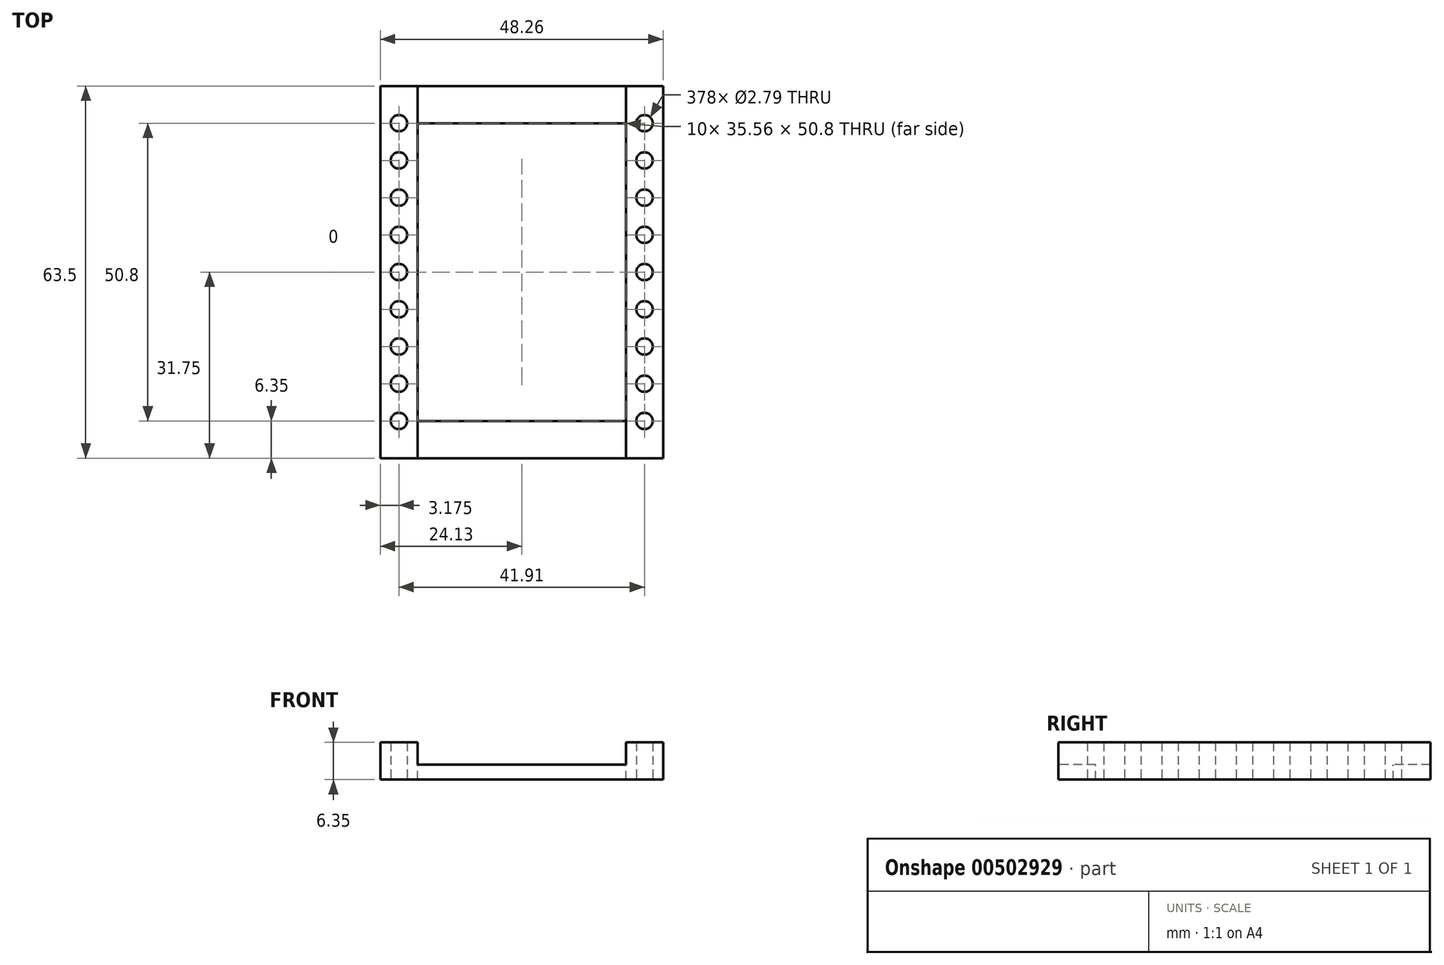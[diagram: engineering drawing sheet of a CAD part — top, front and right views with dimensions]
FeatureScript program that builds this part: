
annotation { "Feature Type Name" : "Feature", "Feature Type Description" : "" }
export const myFeature = defineFeature(function(context is Context, id is Id, definition is map)
    precondition{}
    {
        {
            var Q0;
            Q0=qCreatedBy(makeId("Top.planeOp"),FACE);
            var sketch = newSketch(context, id + "F0", { "sketchPlane" : qUnion([Q0])});
            skCircle(sketch, "E0", {"center": v(-20.96, 0) * mm, "radius": 1.4 * mm});
            skCircle(sketch, "E1", {"center": v(20.96, 0) * mm, "radius": 1.4 * mm});
            skCircle(sketch, "E2.0.1.0", {"center": v(-20.96, 6.35) * mm, "radius": 1.4 * mm});
            skCircle(sketch, "E2.0.1.1", {"center": v(20.96, 6.35) * mm, "radius": 1.4 * mm});
            skCircle(sketch, "E2.0.2.0", {"center": v(-20.96, 12.7) * mm, "radius": 1.4 * mm});
            skCircle(sketch, "E2.0.2.1", {"center": v(20.96, 12.7) * mm, "radius": 1.4 * mm});
            skCircle(sketch, "E2.0.3.0", {"center": v(-20.96, 19.05) * mm, "radius": 1.4 * mm});
            skCircle(sketch, "E2.0.3.1", {"center": v(20.96, 19.05) * mm, "radius": 1.4 * mm});
            skCircle(sketch, "E2.0.4.0", {"center": v(-20.96, 25.4) * mm, "radius": 1.4 * mm});
            skCircle(sketch, "E2.0.4.1", {"center": v(20.96, 25.4) * mm, "radius": 1.4 * mm});
            skLineSegment(sketch, "E2.direction1", {"start": v(-20.96, 0) * mm, "end": v(2.41, 0) * mm, "construction": true});
            skLineSegment(sketch, "E2.direction2", {"start": v(-20.96, 0) * mm, "end": v(-20.96, 6.35) * mm, "construction": true});
            skLineSegment(sketch, "E3", {"start": v(-20.96, 0) * mm, "end": v(-28.33, 0) * mm});
            skCircle(sketch, "E4.MirrorC", {"center": v(-20.96, -6.35) * mm, "radius": 1.4 * mm});
            skCircle(sketch, "E5.MirrorC", {"center": v(20.96, -6.35) * mm, "radius": 1.4 * mm});
            skCircle(sketch, "E6.MirrorC", {"center": v(-20.96, -12.7) * mm, "radius": 1.4 * mm});
            skCircle(sketch, "E7.MirrorC", {"center": v(20.96, -12.7) * mm, "radius": 1.4 * mm});
            skCircle(sketch, "E8.MirrorC", {"center": v(-20.96, -19.05) * mm, "radius": 1.4 * mm});
            skCircle(sketch, "E9.MirrorC", {"center": v(20.96, -19.05) * mm, "radius": 1.4 * mm});
            skCircle(sketch, "E10.MirrorC", {"center": v(-20.96, -25.4) * mm, "radius": 1.4 * mm});
            skCircle(sketch, "E11.MirrorC", {"center": v(20.96, -25.4) * mm, "radius": 1.4 * mm});
            skLineSegment(sketch, "E12.bottom", {"start": v(-17.78, 31.75) * mm, "end": v(-24.13, 31.75) * mm});
            skLineSegment(sketch, "E12.top", {"start": v(-17.78, -31.75) * mm, "end": v(-24.13, -31.75) * mm});
            skLineSegment(sketch, "E12.right", {"start": v(-24.13, 31.75) * mm, "end": v(-24.13, -31.75) * mm});
            skLineSegment(sketch, "E13", {"start": v(0, 0) * mm, "end": v(0, 6.29) * mm});
            skLineSegment(sketch, "E14.MirrorCS", {"start": v(17.78, 31.75) * mm, "end": v(24.13, 31.75) * mm});
            skLineSegment(sketch, "E15.MirrorCS", {"start": v(24.13, 31.75) * mm, "end": v(24.13, -31.75) * mm});
            skLineSegment(sketch, "E16.MirrorCS", {"start": v(17.78, -31.75) * mm, "end": v(24.13, -31.75) * mm});
            skLineSegment(sketch, "E17", {"start": v(-17.78, 31.75) * mm, "end": v(17.78, 31.75) * mm});
            skLineSegment(sketch, "E18", {"start": v(17.78, -31.75) * mm, "end": v(-17.78, -31.75) * mm});
            skPoint(sketch, "E19.MirrorCS.start.orphan", {"position": v(17.78, 31.75) * mm});
            skSolve(sketch);
        }
        {
            var Q0;
            Q0 = qSketchRegion(id + "F0", true);
            extrude(context, id + "F1", {"entities" : qUnion([Q0]), "depth" : 6.35 * mm});
        }
        {
            var Q0;
            Q0=makeQuery(id+"F1.opExtrude","CAP_FACE",FACE,{"disambiguationData":[OSD([sQuery(id+"F0.wireOp",EDGE,"E0"),sQuery(id+"F0.wireOp",EDGE,"E1"),sQuery(id+"F0.wireOp",EDGE,"E2.0.1.0"),sQuery(id+"F0.wireOp",EDGE,"E2.0.1.1"),sQuery(id+"F0.wireOp",EDGE,"E2.0.2.0"),sQuery(id+"F0.wireOp",EDGE,"E2.0.2.1"),sQuery(id+"F0.wireOp",EDGE,"E2.0.3.0"),sQuery(id+"F0.wireOp",EDGE,"E2.0.3.1"),sQuery(id+"F0.wireOp",EDGE,"E2.0.4.0"),sQuery(id+"F0.wireOp",EDGE,"E2.0.4.1"),sQuery(id+"F0.wireOp",EDGE,"E4.MirrorC"),sQuery(id+"F0.wireOp",EDGE,"E5.MirrorC"),sQuery(id+"F0.wireOp",EDGE,"E6.MirrorC"),sQuery(id+"F0.wireOp",EDGE,"E7.MirrorC"),sQuery(id+"F0.wireOp",EDGE,"E8.MirrorC"),sQuery(id+"F0.wireOp",EDGE,"E9.MirrorC"),sQuery(id+"F0.wireOp",EDGE,"E10.MirrorC"),sQuery(id+"F0.wireOp",EDGE,"E11.MirrorC"),sQuery(id+"F0.wireOp",EDGE,"E12.bottom"),sQuery(id+"F0.wireOp",EDGE,"E12.top"),sQuery(id+"F0.wireOp",EDGE,"E12.right"),sQuery(id+"F0.wireOp",EDGE,"E14.MirrorCS"),sQuery(id+"F0.wireOp",EDGE,"E15.MirrorCS"),sQuery(id+"F0.wireOp",EDGE,"E16.MirrorCS"),sQuery(id+"F0.wireOp",EDGE,"E17"),sQuery(id+"F0.wireOp",EDGE,"E18")])],"isStart":false});
            var sketch = newSketch(context, id + "F2", { "sketchPlane" : qUnion([Q0])});
            skLineSegment(sketch, "E20.bottom", {"start": v(17.78, 31.75) * mm, "end": v(-17.78, 31.75) * mm});
            skLineSegment(sketch, "E20.top", {"start": v(17.78, -31.75) * mm, "end": v(-17.78, -31.75) * mm});
            skLineSegment(sketch, "E20.left", {"start": v(17.78, 31.75) * mm, "end": v(17.78, -31.75) * mm});
            skLineSegment(sketch, "E20.right", {"start": v(-17.78, 31.75) * mm, "end": v(-17.78, -31.75) * mm});
            skPoint(sketch, "E20.middle", {"position": v(0, 0) * mm});
            skSolve(sketch);
        }
        {
            var Q0;
            Q0 = qSketchRegion(id + "F2", true);
            extrude(context, id + "F3", {"entities" : qUnion([Q0]), "operationType" : NewBodyOperationType.REMOVE, "oppositeDirection" : true, "depth" : 3.8 * mm});
        }
        {
            var Q0;
            Q0=makeQuery(id+"F3.boolean.opBoolean","COPY",FACE,{"derivedFrom":makeQuery(id+"F3.opExtrude","CAP_FACE",FACE,{"disambiguationData":[OSD([sQuery(id+"F2.wireOp",EDGE,"E20.bottom"),sQuery(id+"F2.wireOp",EDGE,"E20.top"),sQuery(id+"F2.wireOp",EDGE,"E20.left"),sQuery(id+"F2.wireOp",EDGE,"E20.right")])],"isStart":false})});
            var sketch = newSketch(context, id + "F4", { "sketchPlane" : qUnion([Q0])});
            skLineSegment(sketch, "E21.bottom", {"start": v(17.78, 25.4) * mm, "end": v(-17.78, 25.4) * mm});
            skLineSegment(sketch, "E21.top", {"start": v(17.78, -25.4) * mm, "end": v(-17.78, -25.4) * mm});
            skLineSegment(sketch, "E21.left", {"start": v(17.78, 25.4) * mm, "end": v(17.78, -25.4) * mm});
            skLineSegment(sketch, "E21.right", {"start": v(-17.78, 25.4) * mm, "end": v(-17.78, -25.4) * mm});
            skPoint(sketch, "E21.middle", {"position": v(0, 0) * mm});
            skSolve(sketch);
        }
        {
            var Q0;
            Q0 = qSketchRegion(id + "F4", true);
            extrude(context, id + "F5", {"entities" : qUnion([Q0]), "operationType" : NewBodyOperationType.REMOVE, "oppositeDirection" : true, "depth" : 25.4 * mm});
        }
    });
